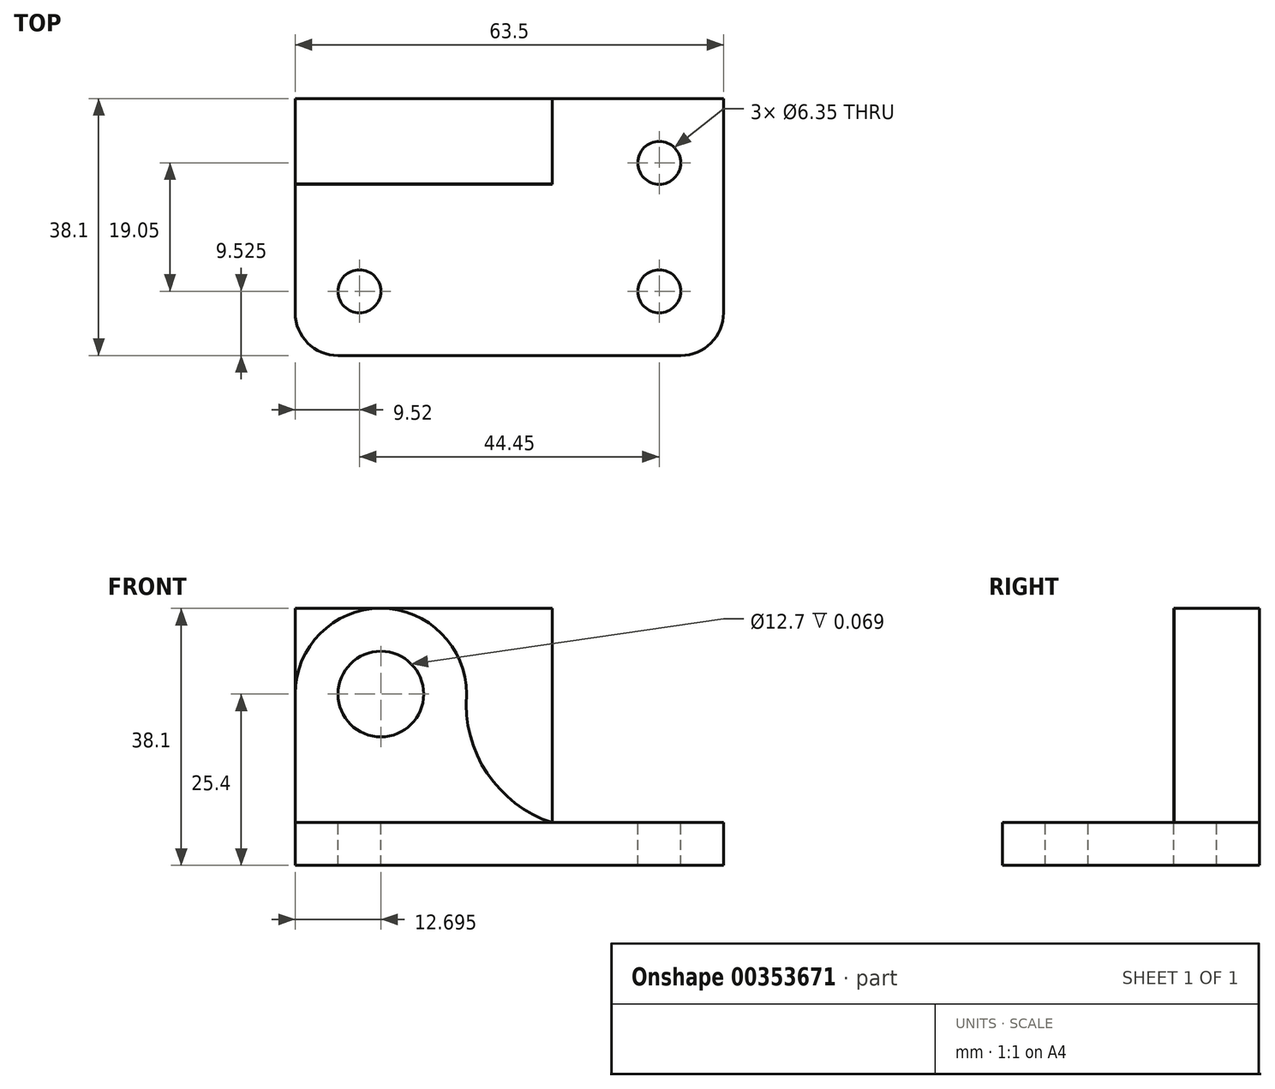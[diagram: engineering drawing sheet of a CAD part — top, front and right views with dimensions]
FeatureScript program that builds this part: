
annotation { "Feature Type Name" : "Feature", "Feature Type Description" : "" }
export const myFeature = defineFeature(function(context is Context, id is Id, definition is map)
    precondition{}
    {
        {
            var Q0;
            Q0=qCreatedBy(makeId("Top.planeOp"),FACE);
            var sketch = newSketch(context, id + "F0", { "sketchPlane" : qUnion([Q0])});
            skLineSegment(sketch, "E0", {"start": v(-42.65, 38.1) * mm, "end": v(-42.65, 0) * mm});
            skLineSegment(sketch, "E1", {"start": v(-42.65, 0) * mm, "end": v(20.85, 0) * mm});
            skLineSegment(sketch, "E2", {"start": v(20.85, 0) * mm, "end": v(20.85, 38.1) * mm});
            skLineSegment(sketch, "E3", {"start": v(20.85, 38.1) * mm, "end": v(-42.65, 38.1) * mm});
            skSolve(sketch);
        }
        {
            var Q0;
            Q0=makeQuery(id+"F0.imprint","IMPRINT",FACE,{"disambiguationData":[TD([[makeQuery(id+"F0.imprint","IMPRINT",EDGE,{"derivedFrom":sQuery(id+"F0.wireOp",EDGE,"E0")}),1.0]])]});
            extrude(context, id + "F1", {"entities" : qUnion([Q0]), "depth" : 38.1 * mm});
        }
        {
            var Q0;
            Q0=makeQuery(id+"F1.opExtrude","CAP_FACE",FACE,{"disambiguationData":[OSD([sQuery(id+"F0.wireOp",EDGE,"E0"),sQuery(id+"F0.wireOp",EDGE,"E1"),sQuery(id+"F0.wireOp",EDGE,"E2"),sQuery(id+"F0.wireOp",EDGE,"E3")])],"isStart":false});
            var sketch = newSketch(context, id + "F2", { "sketchPlane" : qUnion([Q0])});
            skLineSegment(sketch, "E4", {"start": v(-42.65, 25.4) * mm, "end": v(-4.55, 25.4) * mm});
            skLineSegment(sketch, "E5", {"start": v(-4.55, 25.4) * mm, "end": v(-4.55, 38.1) * mm});
            skSolve(sketch);
        }
        {
            var Q0;
            Q0 = qSketchRegion(id + "F2", true);
            var Q1;
            {var subQ3=sQuery(id+"F2.wireOp",EDGE,"E4");Q1=makeQuery(id+"F2.imprint","IMPRINT",FACE,{"disambiguationData":[TD([[makeQuery(id+"F2.imprint","IMPRINT",EDGE,{"derivedFrom":subQ3}),-1.0]])]});}
            extrude(context, id + "F3", {"entities" : qUnion([Q0, Q1]), "operationType" : NewBodyOperationType.REMOVE, "oppositeDirection" : true, "depth" : 31.75 * mm});
        }
        {
            var Q0;
            Q0=makeQuery(id+"F3.boolean.opBoolean","COPY",FACE,{"derivedFrom":makeQuery(id+"F3.opExtrude","SWEPT_FACE",FACE,{"disambiguationData":[OSD([sQuery(id+"F2.wireOp",EDGE,"E4")])]})});
            var sketch = newSketch(context, id + "F4", { "sketchPlane" : qUnion([Q0])});
            skCircle(sketch, "E6", {"center": v(-29.95, 25.4) * mm, "radius": 6.35 * mm});
            skArc(sketch, "E7", {"start": v(-17.25, 25.4) * mm, "mid": v(-29.95, 38.1) * mm, "end": v(-42.65, 25.4) * mm});
            skArc(sketch, "E8", {"start": v(-17.25, 25.4) * mm, "mid": v(-14.2, 13.68) * mm, "end": v(-4.55, 6.35) * mm});
            skSolve(sketch);
        }
        {
            var Q0;
            Q0 = qSketchRegion(id + "F4", true);
            var Q1;
            {var subQ0=sQuery(id+"F4.wireOp",EDGE,"E7");var subQ1=sQuery(id+"F2.wireOp",EDGE,"E4");var subQ4=makeQuery(id+"F3.boolean.opBoolean","COPY",EDGE,{"derivedFrom":makeQuery(id+"F3.opExtrude","CAP_EDGE",EDGE,{"disambiguationData":[OSD([subQ1])],"isStart":true})});var subQ5=makeQuery(id+"F4.imprint","INTERSECT",VERTEX,{"derivedFrom":[subQ4,subQ0]});Q1=makeQuery(id+"F4.imprint","IMPRINT",FACE,{"disambiguationData":[TD([[makeQuery(id+"F4.imprint","IMPRINT",EDGE,{"disambiguationData":[TD([[subQ5,-1.0]])],"derivedFrom":subQ0}),-1.0]])]});}
            var Q2;
            {var subQ0=sQuery(id+"F4.wireOp",EDGE,"E8");Q2=makeQuery(id+"F4.imprint","IMPRINT",FACE,{"disambiguationData":[TD([[makeQuery(id+"F4.imprint","IMPRINT",EDGE,{"derivedFrom":subQ0}),1.0]])]});}
            extrude(context, id + "F5", {"entities" : qUnion([Q0, Q1, Q2]), "operationType" : NewBodyOperationType.REMOVE, "oppositeDirection" : true, "depth" : 7 / 101.6 * mm});
        }
        {
            var Q0;
            Q0=makeQuery(id+"F3.boolean.opBoolean","COPY",FACE,{"derivedFrom":makeQuery(id+"F3.opExtrude","CAP_FACE",FACE,{"disambiguationData":[OSD([sQuery(id+"F0.wireOp",EDGE,"E0"),sQuery(id+"F0.wireOp",EDGE,"E1"),sQuery(id+"F0.wireOp",EDGE,"E2"),sQuery(id+"F0.wireOp",EDGE,"E3"),sQuery(id+"F2.wireOp",EDGE,"E4"),sQuery(id+"F2.wireOp",EDGE,"E5")])],"isStart":false})});
            var sketch = newSketch(context, id + "F6", { "sketchPlane" : qUnion([Q0])});
            skCircle(sketch, "E9", {"center": v(11.32, 28.58) * mm, "radius": 3.18 * mm});
            skCircle(sketch, "E10", {"center": v(11.32, 9.53) * mm, "radius": 3.18 * mm});
            skCircle(sketch, "E11", {"center": v(-33.13, 9.53) * mm, "radius": 3.18 * mm});
            skSolve(sketch);
        }
        {
            var Q0;
            Q0=makeQuery(id+"F6.imprint","IMPRINT",FACE,{"disambiguationData":[TD([[makeQuery(id+"F6.imprint","IMPRINT",EDGE,{"derivedFrom":sQuery(id+"F6.wireOp",EDGE,"E10")}),1.0]])]});
            var Q1;
            Q1=makeQuery(id+"F6.imprint","IMPRINT",FACE,{"disambiguationData":[TD([[makeQuery(id+"F6.imprint","IMPRINT",EDGE,{"derivedFrom":sQuery(id+"F6.wireOp",EDGE,"E11")}),1.0]])]});
            var Q2;
            Q2=makeQuery(id+"F6.imprint","IMPRINT",FACE,{"disambiguationData":[TD([[makeQuery(id+"F6.imprint","IMPRINT",EDGE,{"derivedFrom":sQuery(id+"F6.wireOp",EDGE,"E9")}),1.0]])]});
            extrude(context, id + "F7", {"entities" : qUnion([Q0, Q1, Q2]), "operationType" : NewBodyOperationType.REMOVE, "oppositeDirection" : true, "depth" : 25.4 * mm});
        }
        {
            var Q0;
            Q0=makeQuery(id+"F3.boolean.opBoolean","COPY",FACE,{"derivedFrom":makeQuery(id+"F3.opExtrude","CAP_FACE",FACE,{"disambiguationData":[OSD([sQuery(id+"F0.wireOp",EDGE,"E0"),sQuery(id+"F0.wireOp",EDGE,"E1"),sQuery(id+"F0.wireOp",EDGE,"E2"),sQuery(id+"F0.wireOp",EDGE,"E3"),sQuery(id+"F2.wireOp",EDGE,"E4"),sQuery(id+"F2.wireOp",EDGE,"E5")])],"isStart":false})});
            var sketch = newSketch(context, id + "F8", { "sketchPlane" : qUnion([Q0])});
            skLineSegment(sketch, "E12", {"start": v(-42.65, 8.14) * mm, "end": v(-42.65, 6.35) * mm});
            skLineSegment(sketch, "E13", {"start": v(-36.3, 0) * mm, "end": v(-32.14, 0) * mm});
            skPoint(sketch, "E14.visualSharp", {"position": v(-42.65, 0) * mm});
            skArc(sketch, "E14.filletArc", {"start": v(-42.65, 6.35) * mm, "mid": v(-40.8, 1.86) * mm, "end": v(-36.3, 0) * mm});
            skSolve(sketch);
        }
        {
            var Q0;
            Q0 = qSketchRegion(id + "F8", true);
            var Q1;
            {var subQ0=sQuery(id+"F8.wireOp",EDGE,"E14.filletArc");Q1=makeQuery(id+"F8.imprint","IMPRINT",FACE,{"disambiguationData":[TD([[makeQuery(id+"F8.imprint","IMPRINT",EDGE,{"derivedFrom":subQ0}),-1.0]])]});}
            extrude(context, id + "F9", {"entities" : qUnion([Q0, Q1]), "operationType" : NewBodyOperationType.REMOVE, "oppositeDirection" : true, "depth" : 25.4 * mm});
        }
        {
            var Q0;
            Q0=makeQuery(id+"F3.boolean.opBoolean","COPY",FACE,{"derivedFrom":makeQuery(id+"F3.opExtrude","CAP_FACE",FACE,{"disambiguationData":[OSD([sQuery(id+"F0.wireOp",EDGE,"E0"),sQuery(id+"F0.wireOp",EDGE,"E1"),sQuery(id+"F0.wireOp",EDGE,"E2"),sQuery(id+"F0.wireOp",EDGE,"E3"),sQuery(id+"F2.wireOp",EDGE,"E4"),sQuery(id+"F2.wireOp",EDGE,"E5")])],"isStart":false})});
            var sketch = newSketch(context, id + "F10", { "sketchPlane" : qUnion([Q0])});
            skLineSegment(sketch, "E15", {"start": v(20.85, 12.12) * mm, "end": v(20.85, 6.35) * mm});
            skLineSegment(sketch, "E16", {"start": v(14.5, 0) * mm, "end": v(14.13, 0) * mm});
            skPoint(sketch, "E17.visualSharp", {"position": v(20.85, 0) * mm});
            skArc(sketch, "E17.filletArc", {"start": v(14.5, 0) * mm, "mid": v(18.99, 1.86) * mm, "end": v(20.85, 6.35) * mm});
            skSolve(sketch);
        }
        {
            var Q0;
            Q0 = qSketchRegion(id + "F10", true);
            var Q1;
            {var subQ0=sQuery(id+"F10.wireOp",EDGE,"E17.filletArc");Q1=makeQuery(id+"F10.imprint","IMPRINT",FACE,{"disambiguationData":[TD([[makeQuery(id+"F10.imprint","IMPRINT",EDGE,{"derivedFrom":subQ0}),-1.0]])]});}
            extrude(context, id + "F11", {"entities" : qUnion([Q0, Q1]), "operationType" : NewBodyOperationType.REMOVE, "oppositeDirection" : true, "depth" : 25.4 * mm});
        }
    });
